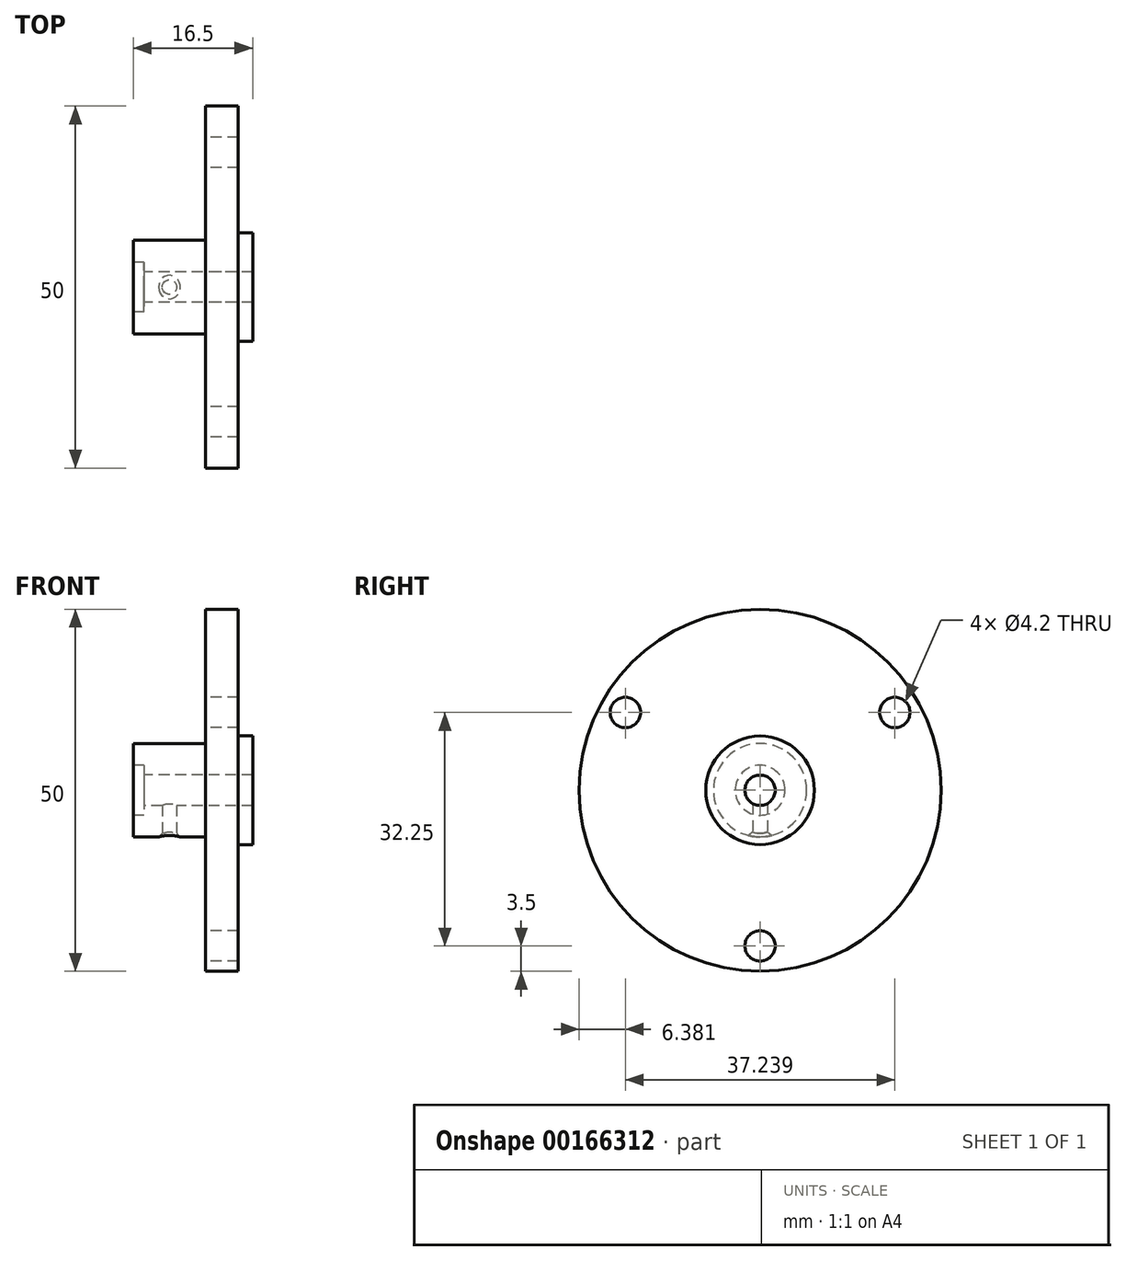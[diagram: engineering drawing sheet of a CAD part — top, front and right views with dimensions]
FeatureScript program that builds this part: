
annotation { "Feature Type Name" : "Feature", "Feature Type Description" : "" }
export const myFeature = defineFeature(function(context is Context, id is Id, definition is map)
    precondition{}
    {
        {
            assignVariable(context, id + "F0", {"name" : "Diam_Left", "anyValue" : 12.9});
        }
        {
            var Q0;
            Q0=qCreatedBy(makeId("Front.planeOp"),FACE);
            var sketch = newSketch(context, id + "F1", { "sketchPlane" : qUnion([Q0])});
            skLineSegment(sketch, "E0", {"start": v(0, 0) * mm, "end": v(25.16, 0) * mm, "construction": true});
            skLineSegment(sketch, "E1", {"start": v(15, 2.1) * mm, "end": v(0, 2.1) * mm});
            skLineSegment(sketch, "E2", {"start": v(0, 2.1) * mm, "end": v(0, 3.45) * mm});
            skLineSegment(sketch, "E3", {"start": v(0, 3.45) * mm, "end": v(-1.5, 3.45) * mm});
            skLineSegment(sketch, "E4", {"start": v(-1.5, 3.45) * mm, "end": v(-1.5, 6.45) * mm});
            skLineSegment(sketch, "E5", {"start": v(-1.5, 6.45) * mm, "end": v(8.5, 6.45) * mm});
            skLineSegment(sketch, "E6", {"start": v(8.5, 6.45) * mm, "end": v(8.5, 25) * mm});
            skLineSegment(sketch, "E7", {"start": v(8.5, 25) * mm, "end": v(13, 25) * mm});
            skLineSegment(sketch, "E8", {"start": v(13, 25) * mm, "end": v(13, 7.5) * mm});
            skLineSegment(sketch, "E9", {"start": v(13, 7.5) * mm, "end": v(15, 7.5) * mm});
            skLineSegment(sketch, "E10", {"start": v(15, 7.5) * mm, "end": v(15, 2.1) * mm});
            skSolve(sketch);
        }
        {
            var Q0;
            Q0=makeQuery(id+"F1.imprint","IMPRINT",FACE,{"disambiguationData":[TD([[makeQuery(id+"F1.imprint","IMPRINT",EDGE,{"derivedFrom":sQuery(id+"F1.wireOp",EDGE,"E1")}),-1.0]])]});
            var Q1;
            Q1=sQuery(id+"F1.wireOp",EDGE,"E0");
            revolve(context, id + "F2", {"entities" : qUnion([Q0]), "axis" : qUnion([Q1]), "revolveType" : RevolveType.FULL});
        }
        {
            var Q0;
            Q0=makeQuery(id+"F2.opRevolve","SWEPT_FACE",FACE,{"disambiguationData":[OSD([sQuery(id+"F1.wireOp",EDGE,"E6")])]});
            var sketch = newSketch(context, id + "F3", { "sketchPlane" : qUnion([Q0])});
            skCircle(sketch, "E11", {"center": v(0, 0) * mm, "radius": 21.5 * mm, "construction": true});
            skCircle(sketch, "E12", {"center": v(-18.62, 10.75) * mm, "radius": 2.1 * mm});
            skCircle(sketch, "E13.1.0", {"center": v(0, -21.5) * mm, "radius": 2.1 * mm});
            skCircle(sketch, "E13.2.0", {"center": v(18.62, 10.75) * mm, "radius": 2.1 * mm});
            skLineSegment(sketch, "E14", {"start": v(-18.62, 10.75) * mm, "end": v(0, 0) * mm, "construction": true});
            skLineSegment(sketch, "E15", {"start": v(0, 0) * mm, "end": v(0, -21.5) * mm, "construction": true});
            skSolve(sketch);
        }
        {
            var Q0;
            Q0=makeQuery(id+"F3.imprint","IMPRINT",FACE,{"disambiguationData":[TD([[makeQuery(id+"F3.imprint","IMPRINT",EDGE,{"derivedFrom":sQuery(id+"F3.wireOp",EDGE,"E12")}),1.0]])]});
            var Q1;
            Q1=makeQuery(id+"F3.imprint","IMPRINT",FACE,{"disambiguationData":[TD([[makeQuery(id+"F3.imprint","IMPRINT",EDGE,{"derivedFrom":sQuery(id+"F3.wireOp",EDGE,"E13.2.0")}),1.0]])]});
            var Q2;
            Q2=makeQuery(id+"F3.imprint","IMPRINT",FACE,{"disambiguationData":[TD([[makeQuery(id+"F3.imprint","IMPRINT",EDGE,{"derivedFrom":sQuery(id+"F3.wireOp",EDGE,"E13.1.0")}),1.0]])]});
            extrude(context, id + "F4", {"entities" : qUnion([Q0, Q1, Q2]), "operationType" : NewBodyOperationType.REMOVE, "endBound" : BoundingType.THROUGH_ALL, "oppositeDirection" : true, "depth" : 25 * mm});
        }
        {
            var Q0;
            Q0=qCreatedBy(makeId("Top.planeOp"),FACE);
            cPlane(context, id + "F5", {"entities" : qUnion([Q0]), "cplaneType" : CPlaneType.OFFSET, "offset" : (getVariable(context, 'Diam_Left') / 2) * mm, "oppositeDirection" : true, "width" : 150 * mm, "height" : 150 * mm});
        }
        {
            var Q0;
            Q0=qCreatedBy(id+"F5.planeOp",FACE);
            var sketch = newSketch(context, id + "F6", { "sketchPlane" : qUnion([Q0])});
            skCircle(sketch, "E16", {"center": v(3.5, 0) * mm, "radius": 1 * mm});
            skSolve(sketch);
        }
        {
            var Q0;
            Q0=makeQuery(id+"F6.imprint","IMPRINT",FACE,{"disambiguationData":[TD([[makeQuery(id+"F6.imprint","IMPRINT",EDGE,{"derivedFrom":sQuery(id+"F6.wireOp",EDGE,"E16")}),1.0]])]});
            extrude(context, id + "F7", {"entities" : qUnion([Q0]), "operationType" : NewBodyOperationType.REMOVE, "depth" : (getVariable(context, 'Diam_Left') / 2) * mm});
        }
        {
            var Q0;
            Q0=makeQuery(id+"F7.boolean.opBoolean","INTERSECT",EDGE,{"derivedFrom":[makeQuery(id+"F2.opRevolve","SWEPT_FACE",FACE,{"disambiguationData":[OSD([sQuery(id+"F1.wireOp",EDGE,"E5")])]}),makeQuery(id+"F7.opExtrude","SWEPT_FACE",FACE,{"disambiguationData":[OSD([sQuery(id+"F6.wireOp",EDGE,"E16")])]})]});
            chamfer(context, id + "F8", {"entities" : qUnion([Q0]), "width" : 0.5 * mm, "tangentPropagation" : true});
        }
    });
